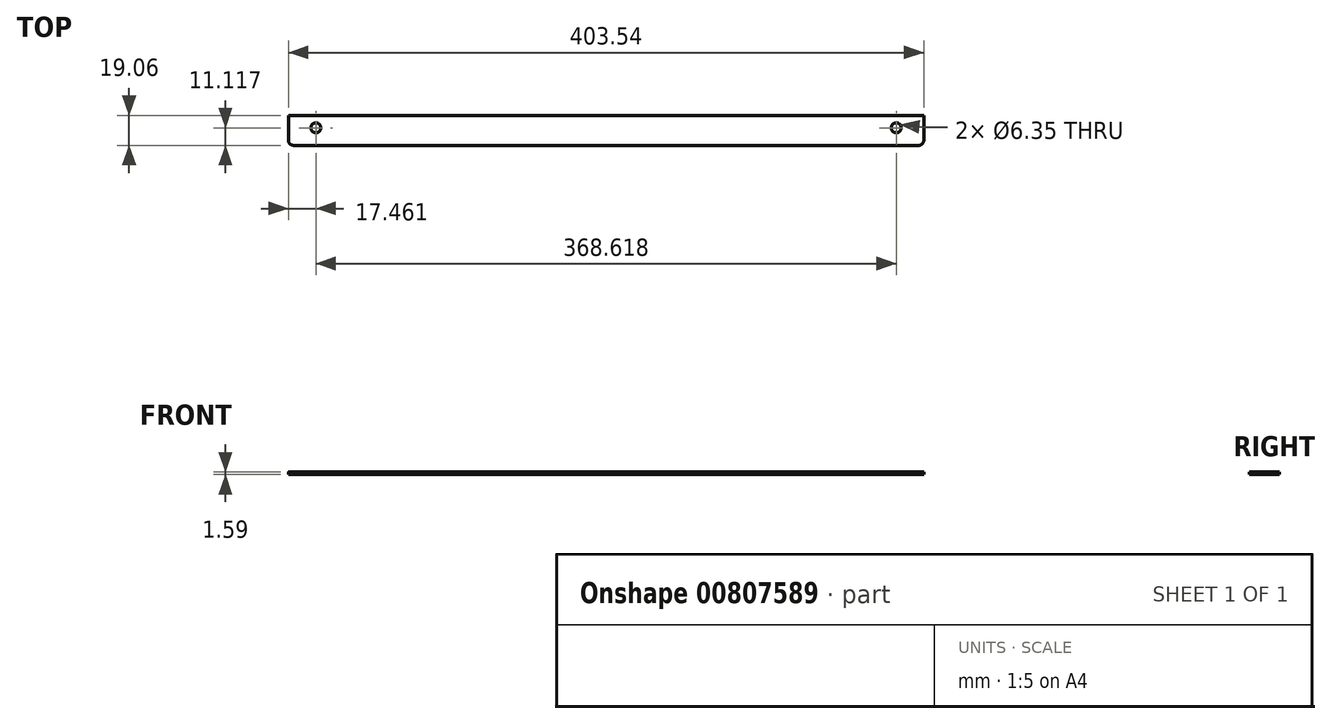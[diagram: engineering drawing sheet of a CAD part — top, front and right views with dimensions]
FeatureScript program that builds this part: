
annotation { "Feature Type Name" : "Feature", "Feature Type Description" : "" }
export const myFeature = defineFeature(function(context is Context, id is Id, definition is map)
    precondition{}
    {
        {
            var Q0;
            Q0=qCreatedBy(makeId("Top.planeOp"),FACE);
            var sketch = newSketch(context, id + "F0", { "sketchPlane" : qUnion([Q0])});
            skLineSegment(sketch, "E0.bottom", {"start": v(-201.77, 9.52) * mm, "end": v(201.77, 9.52) * mm});
            skLineSegment(sketch, "E0.top", {"start": v(-198.6, -9.52) * mm, "end": v(198.6, -9.52) * mm});
            skLineSegment(sketch, "E0.left", {"start": v(-201.77, 9.52) * mm, "end": v(-201.77, -6.35) * mm});
            skLineSegment(sketch, "E0.right", {"start": v(201.77, 9.52) * mm, "end": v(201.77, -6.35) * mm});
            skPoint(sketch, "E0.middle", {"position": v(0, 0) * mm});
            skArc(sketch, "E1", {"start": v(-198.6, -9.52) * mm, "mid": v(-200.84, -8.6) * mm, "end": v(-201.77, -6.35) * mm});
            skLineSegment(sketch, "E2", {"start": v(0, 24.83) * mm, "end": v(0, -29.93) * mm, "construction": true});
            skArc(sketch, "E3.MirrorCS", {"start": v(198.6, -9.52) * mm, "mid": v(200.84, -8.6) * mm, "end": v(201.77, -6.35) * mm});
            skPoint(sketch, "E4.orphan", {"position": v(-201.77, -9.52) * mm});
            skPoint(sketch, "E5.orphan", {"position": v(201.77, -9.52) * mm});
            skCircle(sketch, "E6", {"center": v(-184.3, 1.59) * mm, "radius": 3.18 * mm});
            skCircle(sketch, "E7.MirrorC", {"center": v(184.3, 1.59) * mm, "radius": 3.18 * mm});
            skSolve(sketch);
        }
        {
            var Q0;
            Q0=makeQuery(id+"F0.imprint","IMPRINT",FACE,{"disambiguationData":[TD([[makeQuery(id+"F0.imprint","IMPRINT",EDGE,{"derivedFrom":sQuery(id+"F0.wireOp",EDGE,"E0.bottom")}),-1.0]])]});
            extrude(context, id + "F1", {"entities" : qUnion([Q0]), "depth" : 1.59 * mm, "offsetDistance" : 25.4 * mm});
        }
    });
